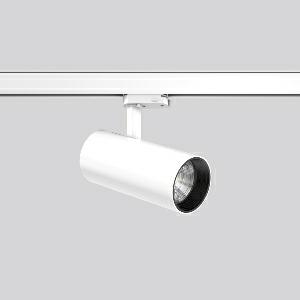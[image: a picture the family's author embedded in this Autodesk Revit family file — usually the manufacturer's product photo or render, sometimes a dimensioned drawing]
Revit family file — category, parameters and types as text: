
# Revit family: deecos_s_mini_742200_002_1_f761
name_source: partatom
category: Lighting Fixtures
units: mm (PartAtom-declared; Revit-internal decimal feet)

## family parameters
Cut with Voids When Loaded = No
Host = Face
Light Source = No
Part Type = Normal
Room Calculation Point = No
Round Connector Dimension = Use Diameter
Shared = No

## types (1)
- DEECOS S mini (1 x LED Modul 940, 2150 lm, 4000)
    Apparent Load = 20 VA
    Approval mark = CE
    CIE Flux Codes = 98 100 100 100 100
    Color Rendering = 92
    Color Temperature = 4000
    Default Elevation = 1800 mm
    Description = Series: DEECOS S mini
LED surface-mounted projector in modern design with no visible cooling ribs. Housing: die-cast aluminium, powder-coated. Rotation range: 356°. Swivel range: 90°. Black plastic ring and recessed LED to prevent glare from the side. Optical assembly with lens made of plastic (polycarbonate) for the best homogeneous light distribution - can be changed without tools. Best colour rendering index Ra>90. With multi adaptor for 3-circuit tracks 230 V. Suitable for Track on ceiling, Wall track. High quality converter without flickering and stroboscopic effect. The following accessories can be mounted without use of tools: interchangeable lenses, decorative glasses, honeycomb louvre, clear and frosted diffusers, white interchangeable plastic ring. 
Colour: traffic white, matt (RAL 9016)
Diameter: 87 mm
Height: 214 mm
Lamp: LED
Socket: without socket
Colour temperature: 4000K
Colour rendering index (CRI): 92
System power: 20 W
Rated luminous flux: 2150 lm
Luminous efficiency: 108 lm/W
Control gear: Regulated power supply
Protection class: I
Type of protection: IP 20
    Height = 214 mm
    Lamp = 1 x LED Modul 940
    Lamp Light Flux = 2150 lm
    Lamp count = 1
    Length = 87 mm
    Lifetime = 50000 h
    Luminous efficacy = 108 lm/W
    Manufacturer = RZB
    ModVariant = No
    Model = 742200.002.1
    Mounting Place = Ceiling
    Mounting Type = Rail mounted
    Number of Poles = 1
    OnlyDefault = Yes
    Power Factor = 1
    Product Name = DEECOS S mini
    Product group = Track mounted projectors
    ProductGroupID = 301
    Protection Class = Protection class I
    Protection Degree = IP 20
    RLX_Detail_Level = 1
    RLX_Emergency_Light_Flux = 0 lm
    RLX_Emergency_Type = 0
    RLX_Emergency_Type_DB = No
    RlxData = <blob elided: 35577 chars, md5=17e747cf>
    Socket = socket
    Standby Power = 0 W
    System Light Flux = 2150 lm
    System Power = 20 W
    Type Comments = Product without accessories
    Type Image = 741930.002.jpg
    URL = http://relux.com
    VarID = ---
    Voltage = 230 V
    Voltage Range = 220-240 V
    Weight = 0.00 kg
    Width = 0 mm  [stored 0 ft]

note: [stored X ft] marks values corroborated as IEEE doubles in the binary element streams (Revit-internal decimal feet)

## geometry (parser evidence)
native form markers: Blend x4, Sweep x11
no freeform markers — native parametric forms only
